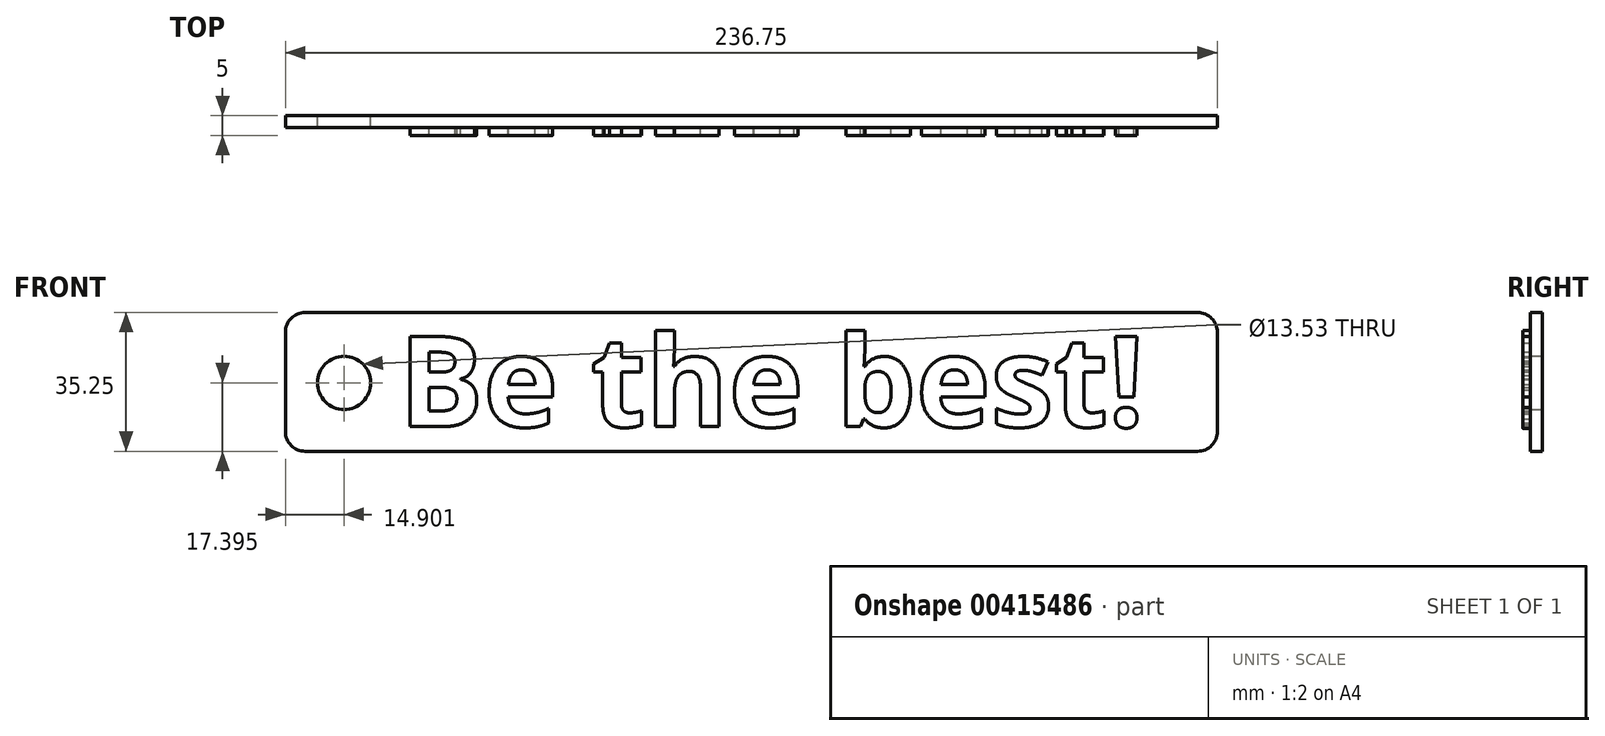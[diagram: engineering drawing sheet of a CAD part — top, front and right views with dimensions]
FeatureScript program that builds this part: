
annotation { "Feature Type Name" : "Feature", "Feature Type Description" : "" }
export const myFeature = defineFeature(function(context is Context, id is Id, definition is map)
    precondition{}
    {
        {
            var Q0;
            Q0=qCreatedBy(makeId("Front.planeOp"),FACE);
            var sketch = newSketch(context, id + "F0", { "sketchPlane" : qUnion([Q0])});
            skLineSegment(sketch, "E0.bottom", {"start": v(-60.4, 37.06) * mm, "end": v(166.6, 37.06) * mm});
            skLineSegment(sketch, "E0.top", {"start": v(-60.4, 1.8) * mm, "end": v(166.6, 1.8) * mm});
            skLineSegment(sketch, "E0.left", {"start": v(-65.4, 32.06) * mm, "end": v(-65.4, 6.8) * mm});
            skLineSegment(sketch, "E0.right", {"start": v(171.35, 32.06) * mm, "end": v(171.35, 6.8) * mm});
            skArc(sketch, "E1.filletArc", {"start": v(171.35, 32.06) * mm, "mid": v(169.89, 35.6) * mm, "end": v(166.35, 37.06) * mm});
            skArc(sketch, "E2.filletArc", {"start": v(166.35, 1.8) * mm, "mid": v(169.89, 3.27) * mm, "end": v(171.35, 6.8) * mm});
            skArc(sketch, "E3.filletArc", {"start": v(-65.4, 6.8) * mm, "mid": v(-63.94, 3.27) * mm, "end": v(-60.4, 1.8) * mm});
            skArc(sketch, "E4.filletArc", {"start": v(-60.4, 37.06) * mm, "mid": v(-63.94, 35.6) * mm, "end": v(-65.4, 32.06) * mm});
            skCircle(sketch, "E5", {"center": v(-50.5, 19.2) * mm, "radius": 6.76 * mm});
            skSolve(sketch);
        }
        {
            var Q0;
            Q0=qCreatedBy(makeId("Front.planeOp"),FACE);
            var sketch = newSketch(context, id + "F1", { "sketchPlane" : qUnion([Q0])});
            skText(sketch, "E6", { "text": "Be the best!", "fontName": "OpenSans-Bold.ttf"});
            const initialGuessF1  = {"E6": [-0.03666, 0.00807, 1, 0, 0.0231]};
            skSetInitialGuess(sketch, initialGuessF1);
            skSolve(sketch);
        }
        {
            var Q0;
            Q0 = qSketchRegion(id + "F0", true);
            extrude(context, id + "F2", {"entities" : qUnion([Q0]), "depth" : 3 * mm, "offsetDistance" : 25 * mm});
        }
        {
            var Q0;
            Q0 = qSketchRegion(id + "F1", true);
            extrude(context, id + "F3", {"entities" : qUnion([Q0]), "operationType" : NewBodyOperationType.ADD, "depth" : 5 * mm, "offsetDistance" : 25 * mm});
        }
    });
